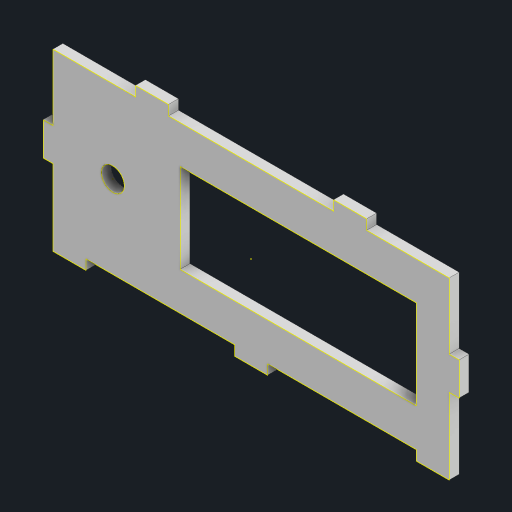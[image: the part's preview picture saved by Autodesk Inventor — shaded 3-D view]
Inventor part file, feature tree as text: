
AUTODESK INVENTOR PART (.ipt)
format: ipt  version: 2023 (Build 270158000, 158)  size: 199,680 bytes
history: native  units: mm
features: sketch x4, extrude x3, projected_geometry x1
ambient origin geometry x8: Origin, YZ Plane, XZ Plane, XY Plane, X Axis, Y Axis, Z Axis, Center Point
bodies: Solid1 (feature_tree)
feature tree (8):
  extrude  "Extrusion1"  Depth=50.0mm
  extrude  "Extrusion2"  Depth=71.5mm
  extrude  "Extrusion3"  Depth=10.0mm
  sketch  "Sketch4"  dims[d7=26.2mm d8=7.0mm d9=8.4mm d10=12.0mm d11=10.0mm d12=3.0mm d13=10.0mm d14=3.0mm d15=10.0mm d16=3.0mm d17=10.0mm d18=3.0mm d19=10.0mm d20=3.0mm d21=10.0mm d22=3.0mm d23=3.0mm d24=10.0mm d25=3.0mm d26=10.0mm d27=3.0mm d28=0.0mm d29=0.0mm d30=0.0mm d31=120.0mm d32=10.0mm d33=3.0mm d34=10.0mm d35=3.0mm d36=30.0mm d37=30.0mm d38=3.0mm d39=0.0mm]
  sketch  "Sketch1"  dims[d0=120.0mm d1=50.0mm]
  sketch  "Sketch2"  dims[d2=27.0mm d3=71.5mm]
  sketch  "Sketch3"  dims[d4=10.0mm d6=18.7mm]
  projected_geometry  "Project Cut Edges1"
